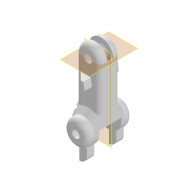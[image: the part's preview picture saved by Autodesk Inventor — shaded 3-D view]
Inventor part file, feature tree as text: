
AUTODESK INVENTOR PART (.ipt)
format: ipt  version: 2020.2 (Build 242310000, 310)  size: 339,456 bytes
history: native  units: mm
features: sketch x9, extrude x5, mirror x3, plane x2, chamfer x2, fillet x2, thread x1, sweep x1
ambient origin geometry x8: Origin, YZ Plane, XZ Plane, XY Plane, X Axis, Y Axis, Z Axis, Center Point
bodies: Solid1 (feature_tree)
feature tree (25):
  extrude  "base"  Depth=10.0mm
  extrude  "joint"  Depth=3.0mm
  plane  "Work Plane1"
  mirror  "Mirror1"
  chamfer  "Chamfer1"  Distance=8.0mm
  extrude  "joint_2"  Depth=10.0mm
  fillet  "Fillet1"  Radius=5.0mm
  plane  "Work Plane2"
  thread  "thread_hole_end"  [1 undecoded]
  extrude  "lock_1"  Depth=9.0mm TaperAngle=0.0deg
  mirror  "Mirror2"
  fillet  "Fillet3"  Radius=2.0mm
  extrude  "lock_2"  Depth=5.25mm
  mirror  "Mirror3"
  chamfer  "Chamfer2"  Distance=25.0mm
  sweep  "Sweep1"
  sketch  "Sketch1"  dims[d0=3.0mm d1=10.0mm]
  sketch  "Sketch2"  dims[d2=24.0mm d3=3.0mm]
  sketch  "Sketch3"  dims[d4=10.0mm d5=8.0mm d6=0.0mm]
  sketch  "Sketch5"  dims[d7=3.0mm d8=10.0mm d9=5.0mm d10=0.0mm d11=2.0mm d12=2.0mm d13=45.0deg]
  sketch  "Sketch6"  dims[d14=10.5mm d15=9.0mm d16=0.0mm d17=2.0mm]
  sketch  "Sketch8"  dims[d21=10.0mm d22=5.25mm]
  sketch  "Sketch9"  dims[d23=3.5mm]
  sketch  "Sketch10"  dims[d24=3.5mm]
  sketch  "Sketch11"  dims[d26=2.5mm d27=25.0mm d28=0.0mm d29=3.5mm d30=2.5mm d31=180.0deg d35=5.0mm d36=3.0mm d37=3.0mm d38=0.0mm d40=3.0mm d41=6.0mm d42=3.0mm d43=13.962634mm d44=3.0mm d45=0.0mm d46=3.0mm d47=2.0mm d48=45.0deg d49=3.5mm d50=10.0mm d52=3.5mm d54=3.0mm d55=0.0mm d56=0.0mm]
note: 1 required parameter value undecoded (feature->parameter linkage not recoverable at this tier; creation-order binding heuristic only, values carry confidence <= 0.55)
